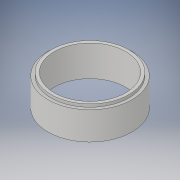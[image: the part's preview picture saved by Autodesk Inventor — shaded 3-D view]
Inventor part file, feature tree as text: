
AUTODESK INVENTOR PART (.ipt)
format: ipt  version: 2017 (Build 210142000, 142)  size: 138,240 bytes
history: native  units: in
note: dims shown in document units (in); Inventor stores cm internally (conversion verified against a paired STEP export)
features: revolve x1, sketch x1
ambient origin geometry x8: Origin, YZ Plane, XZ Plane, XY Plane, X Axis, Y Axis, Z Axis, Center Point
bodies: Body1 (feature_tree)
feature tree (2):
  revolve  "Revolution4"  [1 undecoded]
  sketch  "Sketch1"  dims[d0=1.13in d1=3.4in d2=0.25in d3=0.1718in d5=1.0in d6=1.0in d7=90.0deg d8=0.5in d9=15.0deg d11=0.25in d12=1.25in d13=0.25in d15=0.25in d16=0.5in d17=0.5in d18=0.5in d19=2.5in d20=0.5in d22=0.375in d23=0.25in d25=0.234in d26=15.0deg d30=90.0deg]
note: 1 required parameter value undecoded (feature->parameter linkage not recoverable at this tier; creation-order binding heuristic only, values carry confidence <= 0.55)
